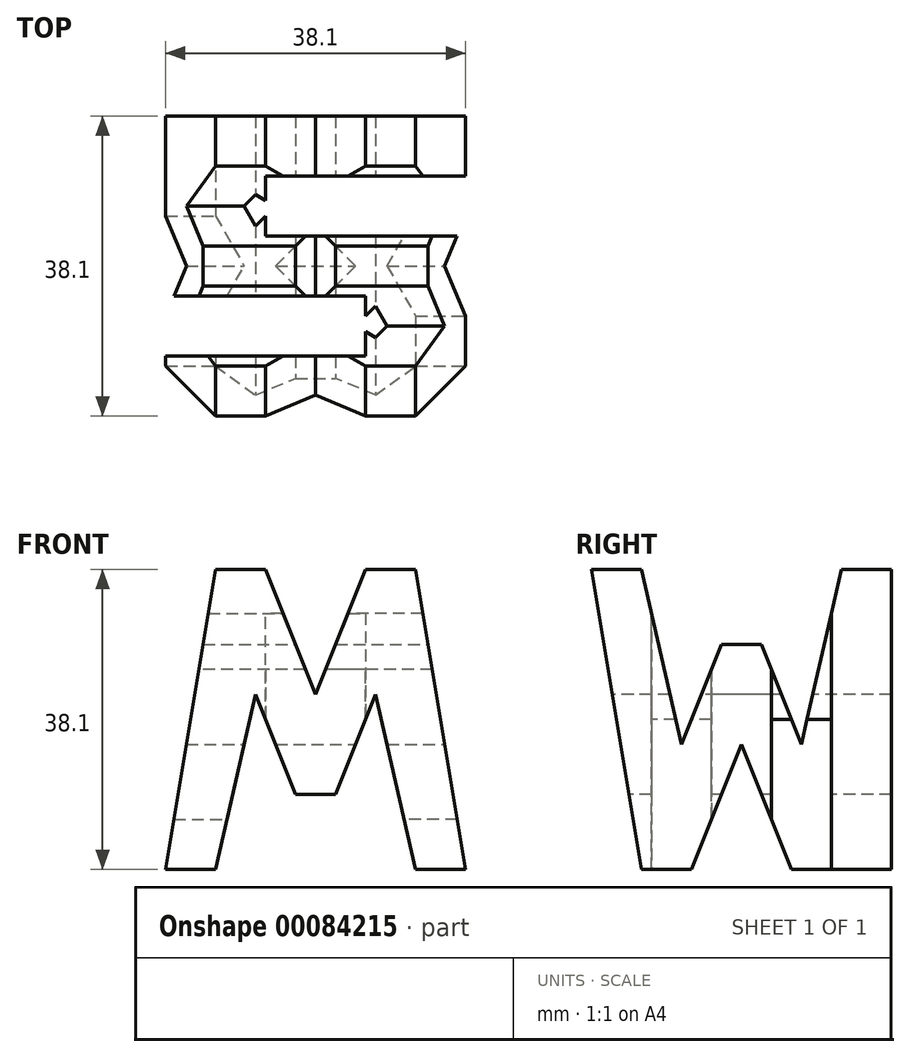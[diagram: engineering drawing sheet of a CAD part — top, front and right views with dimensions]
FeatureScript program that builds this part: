
annotation { "Feature Type Name" : "Feature", "Feature Type Description" : "" }
export const myFeature = defineFeature(function(context is Context, id is Id, definition is map)
    precondition{}
    {
        {
            var Q0;
            Q0=qCreatedBy(makeId("Front.planeOp"),FACE);
            var sketch = newSketch(context, id + "F0", { "sketchPlane" : qUnion([Q0])});
            skLineSegment(sketch, "E0", {"start": v(0, 0) * mm, "end": v(0, 38.1) * mm});
            skLineSegment(sketch, "E1", {"start": v(38.1, 0) * mm, "end": v(0, 0) * mm});
            skLineSegment(sketch, "E2", {"start": v(38.1, 0) * mm, "end": v(38.1, 38.1) * mm});
            skLineSegment(sketch, "E3", {"start": v(0, 38.1) * mm, "end": v(38.1, 38.1) * mm});
            skSolve(sketch);
        }
        {
            var Q0;
            Q0 = qSketchRegion(id + "F0", true);
            extrude(context, id + "F1", {"entities" : qUnion([Q0]), "depth" : 38.1 * mm});
        }
        {
            var Q0;
            Q0=qCreatedBy(makeId("Front.planeOp"),FACE);
            cPlane(context, id + "F2", {"entities" : qUnion([Q0]), "cplaneType" : CPlaneType.OFFSET, "offset" : 38.1 * mm, "width" : 152.4 * mm, "height" : 152.4 * mm});
        }
        {
            var Q0;
            Q0=qCreatedBy(makeId("Right.planeOp"),FACE);
            cPlane(context, id + "F3", {"entities" : qUnion([Q0]), "cplaneType" : CPlaneType.OFFSET, "offset" : 38.1 * mm, "width" : 152.4 * mm, "height" : 152.4 * mm});
        }
        {
            var Q0;
            Q0=qCreatedBy(makeId("Top.planeOp"),FACE);
            cPlane(context, id + "F4", {"entities" : qUnion([Q0]), "cplaneType" : CPlaneType.OFFSET, "offset" : 38.1 * mm, "width" : 152.4 * mm, "height" : 152.4 * mm});
        }
        {
            var Q0;
            Q0=qCreatedBy(id+"F3.planeOp",FACE);
            var sketch = newSketch(context, id + "F5", { "sketchPlane" : qUnion([Q0])});
            skLineSegment(sketch, "E4", {"start": v(0, 0) * mm, "end": v(0, 38.1) * mm});
            skLineSegment(sketch, "E5", {"start": v(0, 0) * mm, "end": v(-38.1, 0) * mm});
            skLineSegment(sketch, "E6", {"start": v(-38.1, 0) * mm, "end": v(-38.1, 38.1) * mm});
            skLineSegment(sketch, "E7", {"start": v(-38.1, 38.1) * mm, "end": v(0, 38.1) * mm});
            skLineSegment(sketch, "E8", {"start": v(0, 38.1) * mm, "end": v(0, 0) * mm});
            skLineSegment(sketch, "E9", {"start": v(-38.1, 38.1) * mm, "end": v(-31.75, 0) * mm});
            skLineSegment(sketch, "E10", {"start": v(-31.75, 38.1) * mm, "end": v(-26.67, 15.88) * mm});
            skLineSegment(sketch, "E11", {"start": v(-26.67, 15.88) * mm, "end": v(-21.6, 28.58) * mm});
            skLineSegment(sketch, "E12", {"start": v(-21.6, 28.58) * mm, "end": v(-16.51, 28.58) * mm});
            skLineSegment(sketch, "E13", {"start": v(-16.51, 28.57) * mm, "end": v(-11.43, 15.88) * mm});
            skLineSegment(sketch, "E14", {"start": v(-11.43, 15.88) * mm, "end": v(-6.35, 38.1) * mm});
            skLineSegment(sketch, "E15", {"start": v(0, 38.1) * mm, "end": v(-6.35, 0) * mm});
            skLineSegment(sketch, "E16", {"start": v(-19.05, 15.88) * mm, "end": v(-25.4, 0) * mm});
            skLineSegment(sketch, "E17", {"start": v(-19.05, 15.88) * mm, "end": v(-12.7, 0) * mm});
            skLineSegment(sketch, "E18", {"start": v(-25.4, 0) * mm, "end": v(-19.05, 0) * mm});
            skSolve(sketch);
        }
        {
            var Q0;
            {var subQ0=sQuery(id+"F5.wireOp",EDGE,"E6");Q0=makeQuery(id+"F5.imprint","IMPRINT",FACE,{"disambiguationData":[TD([[makeQuery(id+"F5.imprint","IMPRINT",EDGE,{"derivedFrom":subQ0}),-1.0]])]});}
            var Q1;
            Q1=makeQuery(id+"F5.imprint","IMPRINT",FACE,{"disambiguationData":[TD([[makeQuery(id+"F5.imprint","IMPRINT",EDGE,{"derivedFrom":sQuery(id+"F5.wireOp",EDGE,"E16")}),1.0]])]});
            var Q2;
            {var subQ0=sQuery(id+"F5.wireOp",EDGE,"E8");Q2=makeQuery(id+"F5.imprint","IMPRINT",FACE,{"disambiguationData":[TD([[makeQuery(id+"F5.imprint","IMPRINT",EDGE,{"derivedFrom":subQ0}),-1.0]])]});}
            var Q3;
            {var subQ0=sQuery(id+"F5.wireOp",EDGE,"E10");Q3=makeQuery(id+"F5.imprint","IMPRINT",FACE,{"disambiguationData":[TD([[makeQuery(id+"F5.imprint","IMPRINT",EDGE,{"derivedFrom":subQ0}),1.0]])]});}
            extrude(context, id + "F6", {"entities" : qUnion([Q0, Q1, Q2, Q3]), "operationType" : NewBodyOperationType.REMOVE, "oppositeDirection" : true, "depth" : 38.1 * mm});
        }
        {
            var Q0;
            Q0=qCreatedBy(id+"F2.planeOp",FACE);
            var sketch = newSketch(context, id + "F7", { "sketchPlane" : qUnion([Q0])});
            skLineSegment(sketch, "E19", {"start": v(0, 0) * mm, "end": v(0, 38.1) * mm});
            skLineSegment(sketch, "E20", {"start": v(0, 38.1) * mm, "end": v(38.1, 38.1) * mm});
            skLineSegment(sketch, "E21", {"start": v(38.1, 38.1) * mm, "end": v(38.1, 0) * mm});
            skLineSegment(sketch, "E22", {"start": v(38.1, 0) * mm, "end": v(0, 0) * mm});
            skLineSegment(sketch, "E23", {"start": v(6.35, 38.1) * mm, "end": v(0, 0) * mm});
            skLineSegment(sketch, "E24", {"start": v(6.35, 0) * mm, "end": v(11.43, 22.23) * mm});
            skLineSegment(sketch, "E25", {"start": v(26.67, 22.23) * mm, "end": v(31.75, 0) * mm});
            skLineSegment(sketch, "E26", {"start": v(38.1, 0) * mm, "end": v(31.75, 38.1) * mm});
            skLineSegment(sketch, "E27", {"start": v(26.67, 22.23) * mm, "end": v(21.59, 9.53) * mm});
            skLineSegment(sketch, "E28", {"start": v(11.43, 22.23) * mm, "end": v(16.51, 9.52) * mm});
            skLineSegment(sketch, "E29", {"start": v(16.51, 9.53) * mm, "end": v(21.59, 9.53) * mm});
            skLineSegment(sketch, "E30", {"start": v(19.05, 22.23) * mm, "end": v(12.7, 38.1) * mm});
            skLineSegment(sketch, "E31", {"start": v(19.05, 22.23) * mm, "end": v(25.4, 38.1) * mm});
            skSolve(sketch);
        }
        {
            var Q0;
            {var subQ0=sQuery(id+"F7.wireOp",EDGE,"E30");Q0=makeQuery(id+"F7.imprint","IMPRINT",FACE,{"disambiguationData":[TD([[makeQuery(id+"F7.imprint","IMPRINT",EDGE,{"derivedFrom":subQ0}),-1.0]])]});}
            var Q1;
            {var subQ1=sQuery(id+"F7.wireOp",EDGE,"E24");Q1=makeQuery(id+"F7.imprint","IMPRINT",FACE,{"disambiguationData":[TD([[makeQuery(id+"F7.imprint","IMPRINT",EDGE,{"derivedFrom":subQ1}),-1.0]])]});}
            var Q2;
            {var subQ0=sQuery(id+"F7.wireOp",EDGE,"E21");Q2=makeQuery(id+"F7.imprint","IMPRINT",FACE,{"disambiguationData":[TD([[makeQuery(id+"F7.imprint","IMPRINT",EDGE,{"derivedFrom":subQ0}),-1.0]])]});}
            var Q3;
            {var subQ0=sQuery(id+"F7.wireOp",EDGE,"E19");Q3=makeQuery(id+"F7.imprint","IMPRINT",FACE,{"disambiguationData":[TD([[makeQuery(id+"F7.imprint","IMPRINT",EDGE,{"derivedFrom":subQ0}),-1.0]])]});}
            extrude(context, id + "F8", {"entities" : qUnion([Q0, Q1, Q2, Q3]), "operationType" : NewBodyOperationType.REMOVE, "oppositeDirection" : true, "depth" : 38.1 * mm});
        }
        {
            var Q0;
            Q0=qCreatedBy(id+"F4.planeOp",FACE);
            var sketch = newSketch(context, id + "F9", { "sketchPlane" : qUnion([Q0])});
            skLineSegment(sketch, "E32", {"start": v(0, 0) * mm, "end": v(38.1, 0) * mm});
            skLineSegment(sketch, "E33", {"start": v(38.1, 0) * mm, "end": v(38.1, -38.1) * mm});
            skLineSegment(sketch, "E34", {"start": v(38.1, -38.1) * mm, "end": v(0, -38.1) * mm});
            skLineSegment(sketch, "E35", {"start": v(0, -38.1) * mm, "end": v(0, 0) * mm});
            skLineSegment(sketch, "E36", {"start": v(12.7, -7.62) * mm, "end": v(38.1, -7.62) * mm});
            skLineSegment(sketch, "E37", {"start": v(12.7, -7.62) * mm, "end": v(12.7, -15.24) * mm});
            skLineSegment(sketch, "E38", {"start": v(12.7, -15.24) * mm, "end": v(38.1, -15.24) * mm});
            skLineSegment(sketch, "E39", {"start": v(0, -22.86) * mm, "end": v(25.4, -22.86) * mm});
            skLineSegment(sketch, "E40", {"start": v(25.4, -22.86) * mm, "end": v(25.4, -30.48) * mm});
            skLineSegment(sketch, "E41", {"start": v(25.4, -30.48) * mm, "end": v(0, -30.48) * mm});
            skSolve(sketch);
        }
        {
            var Q0;
            {var subQ0=sQuery(id+"F9.wireOp",EDGE,"E39");Q0=makeQuery(id+"F9.imprint","IMPRINT",FACE,{"disambiguationData":[TD([[makeQuery(id+"F9.imprint","IMPRINT",EDGE,{"derivedFrom":subQ0}),-1.0]])]});}
            var Q1;
            {var subQ0=sQuery(id+"F9.wireOp",EDGE,"E36");Q1=makeQuery(id+"F9.imprint","IMPRINT",FACE,{"disambiguationData":[TD([[makeQuery(id+"F9.imprint","IMPRINT",EDGE,{"derivedFrom":subQ0}),-1.0]])]});}
            extrude(context, id + "F10", {"entities" : qUnion([Q0, Q1]), "operationType" : NewBodyOperationType.REMOVE, "oppositeDirection" : true, "depth" : 38.1 * mm});
        }
    });
